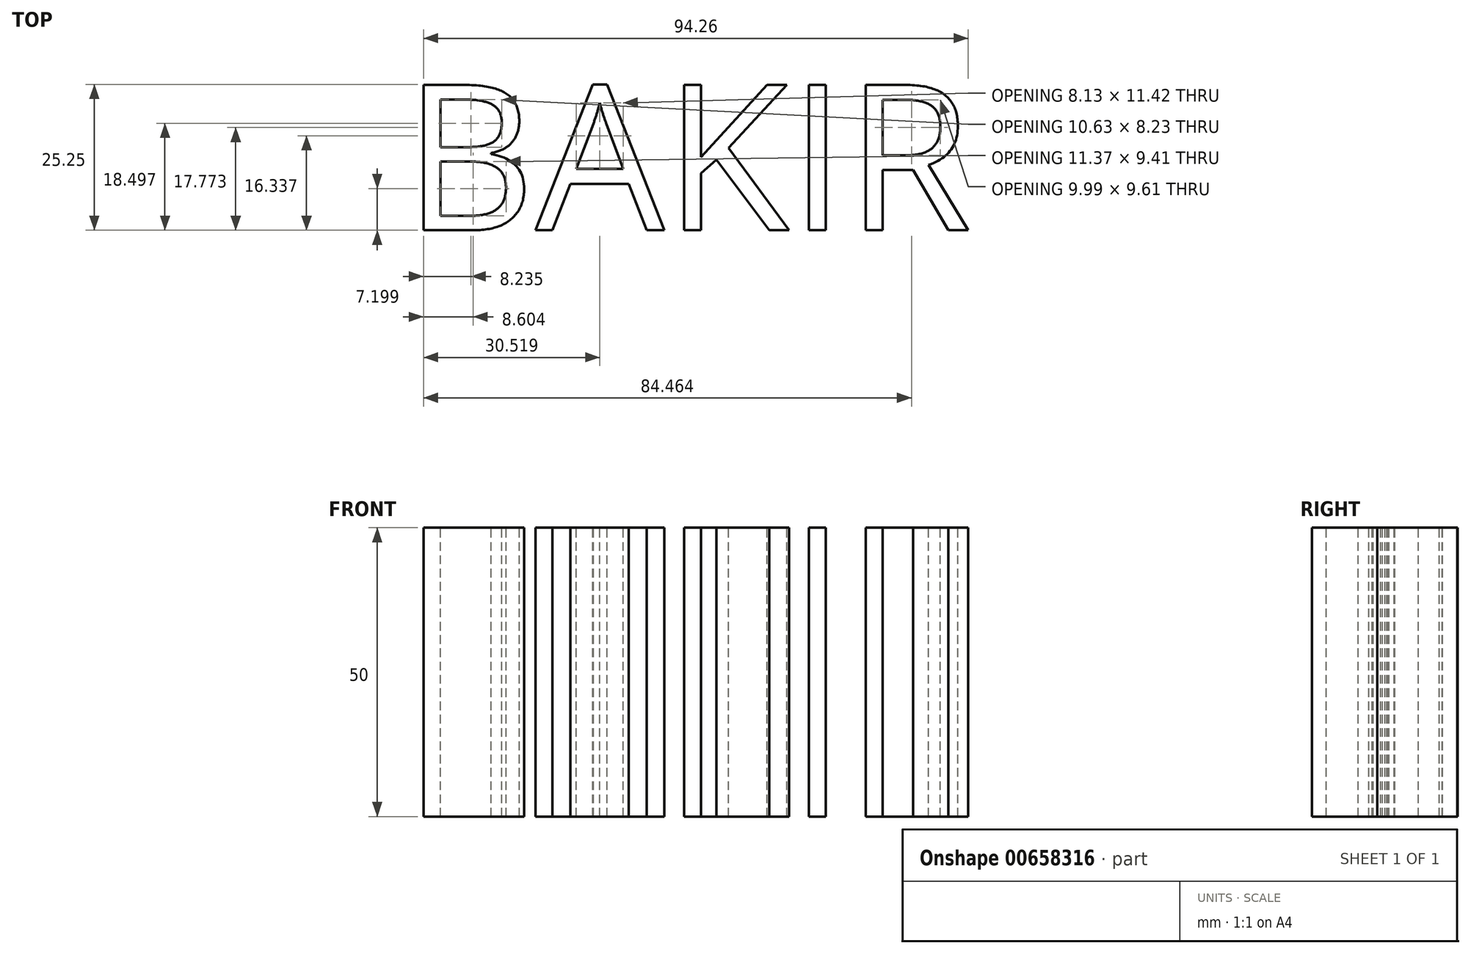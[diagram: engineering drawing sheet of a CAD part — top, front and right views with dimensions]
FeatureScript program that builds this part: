
annotation { "Feature Type Name" : "Feature", "Feature Type Description" : "" }
export const myFeature = defineFeature(function(context is Context, id is Id, definition is map)
    precondition{}
    {
        {
            var Q0;
            Q0=qCreatedBy(makeId("Top.planeOp"),FACE);
            var sketch = newSketch(context, id + "F0", { "sketchPlane" : qUnion([Q0])});
            skText(sketch, "E0", { "text": "BAKIR", "fontName": "OpenSans-Regular.ttf"});
            const initialGuessF0  = {"E0": [-0.06864, 0.02755, 1, 0, 0.02536]};
            skSetInitialGuess(sketch, initialGuessF0);
            skSolve(sketch);
        }
        {
            var Q0;
            Q0 = qSketchRegion(id + "F0", true);
            extrude(context, id + "F1", {"entities" : qUnion([Q0]), "oppositeDirection" : true, "depth" : 50 * mm, "offsetDistance" : 25 * mm});
        }
    });
